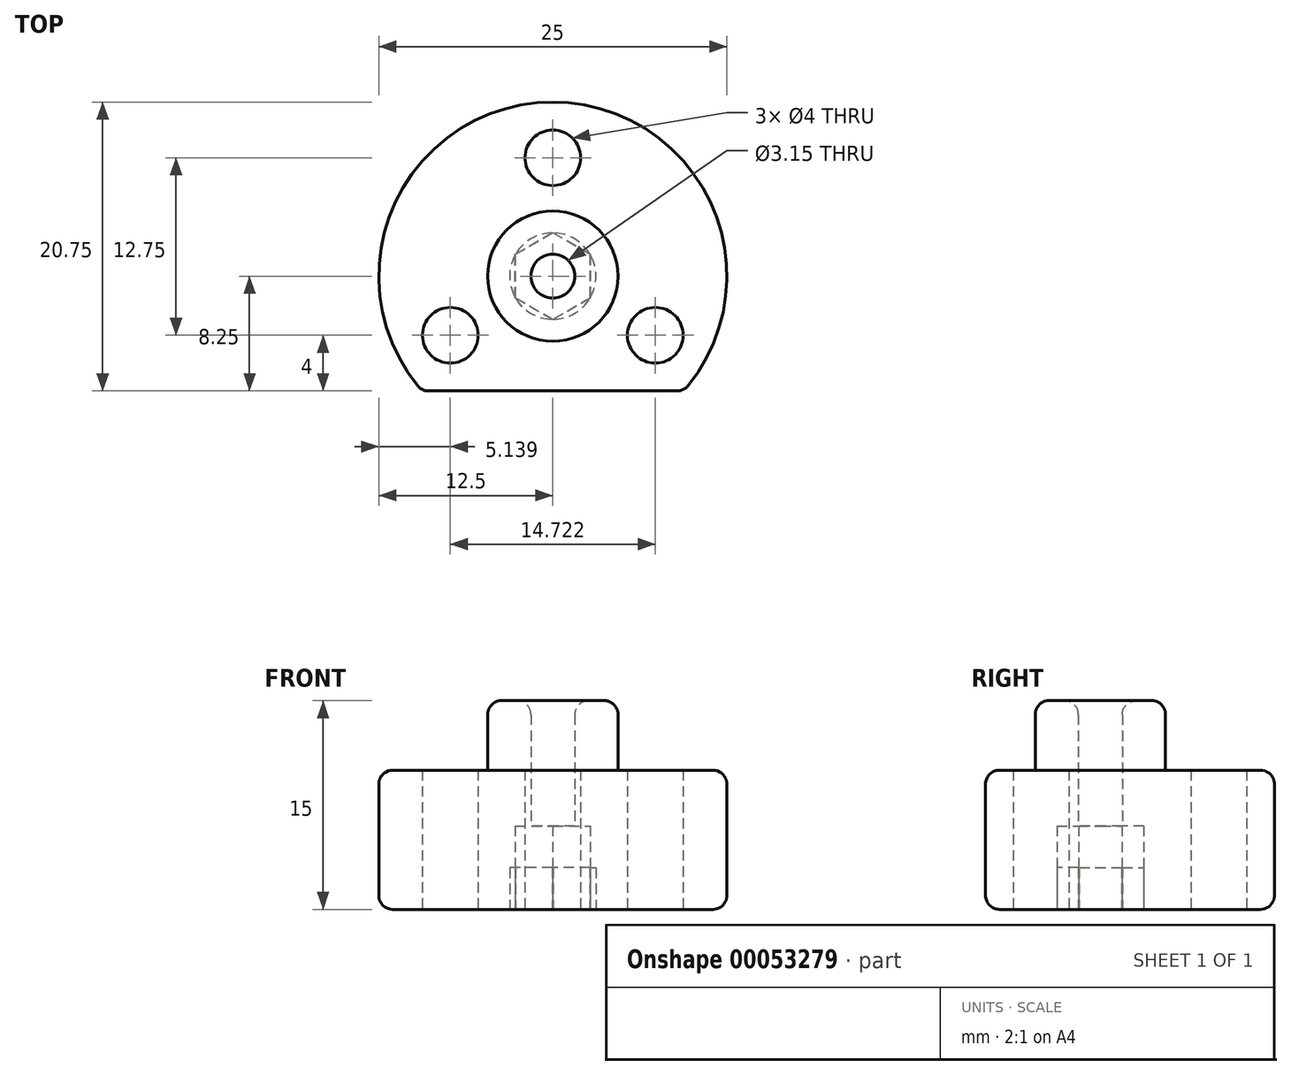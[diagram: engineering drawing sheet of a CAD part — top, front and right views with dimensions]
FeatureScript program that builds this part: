
annotation { "Feature Type Name" : "Feature", "Feature Type Description" : "" }
export const myFeature = defineFeature(function(context is Context, id is Id, definition is map)
    precondition{}
    {
        {
            var Q0;
            Q0=qCreatedBy(makeId("Top.planeOp"),FACE);
            var sketch = newSketch(context, id + "F0", { "sketchPlane" : qUnion([Q0])});
            skCircle(sketch, "E0", {"center": v(0, 0) * mm, "radius": 1.57 * mm});
            skCircle(sketch, "E1", {"center": v(0, 0) * mm, "radius": 8.5 * mm, "construction": true});
            skCircle(sketch, "E2", {"center": v(0, 0) * mm, "radius": 12.5 * mm});
            skCircle(sketch, "E3", {"center": v(0, 8.5) * mm, "radius": 2 * mm});
            skLineSegment(sketch, "E4", {"start": v(0, 0) * mm, "end": v(7.36, -4.25) * mm, "construction": true});
            skLineSegment(sketch, "E5", {"start": v(0, 0) * mm, "end": v(-7.36, -4.25) * mm, "construction": true});
            skLineSegment(sketch, "E6", {"start": v(-8.5, 0) * mm, "end": v(8.5, 0) * mm, "construction": true});
            skCircle(sketch, "E7", {"center": v(7.36, -4.25) * mm, "radius": 2 * mm});
            skCircle(sketch, "E8", {"center": v(-7.36, -4.25) * mm, "radius": 2 * mm});
            skLineSegment(sketch, "E9", {"start": v(7.36, -4.25) * mm, "end": v(7.36, -8.25) * mm, "construction": true});
            skLineSegment(sketch, "E10", {"start": v(-7.36, -4.25) * mm, "end": v(-7.36, -8.25) * mm, "construction": true});
            skLineSegment(sketch, "E11.top", {"start": v(9.4, -8.25) * mm, "end": v(-9.4, -8.25) * mm});
            skCircle(sketch, "E12", {"center": v(0, 0) * mm, "radius": 4.68 * mm});
            skCircle(sketch, "E13", {"center": v(0, 0) * mm, "radius": 3.1 * mm});
            skSolve(sketch);
        }
        {
            var Q0;
            Q0=makeQuery(id+"F0.imprint","IMPRINT",FACE,{"disambiguationData":[TD([[makeQuery(id+"F0.imprint","IMPRINT",EDGE,{"derivedFrom":sQuery(id+"F0.wireOp",EDGE,"E3")}),-1.0]])]});
            extrude(context, id + "F1", {"entities" : qUnion([Q0]), "depth" : 10 * mm});
        }
        {
            var Q0;
            Q0=makeQuery(id+"F0.imprint","IMPRINT",FACE,{"disambiguationData":[TD([[makeQuery(id+"F0.imprint","IMPRINT",EDGE,{"derivedFrom":sQuery(id+"F0.wireOp",EDGE,"E0")}),-1.0]])]});
            var Q1;
            Q1=makeQuery(id+"F0.imprint","IMPRINT",FACE,{"disambiguationData":[TD([[makeQuery(id+"F0.imprint","IMPRINT",EDGE,{"derivedFrom":sQuery(id+"F0.wireOp",EDGE,"E12")}),1.0]])]});
            extrude(context, id + "F2", {"entities" : qUnion([Q0, Q1]), "operationType" : NewBodyOperationType.ADD, "depth" : 15 * mm});
        }
        {
            var Q0;
            Q0=makeQuery(id+"F1.opExtrude","CAP_FACE",FACE,{"disambiguationData":[OSD([sQuery(id+"F0.wireOp",EDGE,"E2"),sQuery(id+"F0.wireOp",EDGE,"E3"),sQuery(id+"F0.wireOp",EDGE,"E7"),sQuery(id+"F0.wireOp",EDGE,"E8"),sQuery(id+"F0.wireOp",EDGE,"E11.top"),sQuery(id+"F0.wireOp",EDGE,"E12")])],"isStart":false});
            var Q1;
            Q1=makeQuery(id+"F0.imprint","IMPRINT",FACE,{"disambiguationData":[TD([[makeQuery(id+"F0.imprint","IMPRINT",EDGE,{"derivedFrom":sQuery(id+"F0.wireOp",EDGE,"E0")}),-1.0]])]});
            extrude(context, id + "F3", {"entities" : qUnion([Q0, Q1]), "operationType" : NewBodyOperationType.REMOVE, "depth" : 3 * mm});
        }
        {
            var Q0;
            Q0=qCreatedBy(makeId("Top.planeOp"),FACE);
            var sketch = newSketch(context, id + "F4", { "sketchPlane" : qUnion([Q0])});
            skCircle(sketch, "E14.cCircle", {"center": v(0, 0) * mm, "radius": 2.7 * mm, "construction": true});
            skLineSegment(sketch, "E14.0", {"start": v(2.7, 1.56) * mm, "end": v(2.7, -1.56) * mm});
            skLineSegment(sketch, "E14.1", {"start": v(2.7, -1.56) * mm, "end": v(0, -3.12) * mm});
            skLineSegment(sketch, "E14.2", {"start": v(0, -3.12) * mm, "end": v(-2.7, -1.56) * mm});
            skLineSegment(sketch, "E14.3", {"start": v(-2.7, -1.56) * mm, "end": v(-2.7, 1.56) * mm});
            skLineSegment(sketch, "E14.4", {"start": v(-2.7, 1.56) * mm, "end": v(0, 3.12) * mm});
            skLineSegment(sketch, "E14.5", {"start": v(0, 3.12) * mm, "end": v(2.7, 1.56) * mm});
            skPoint(sketch, "E14.0.midPoint", {"position": v(2.7, 0) * mm});
            skSolve(sketch);
        }
        {
            var Q0;
            Q0=makeQuery(id+"F4.imprint","IMPRINT",FACE,{"disambiguationData":[TD([[makeQuery(id+"F4.imprint","IMPRINT",EDGE,{"derivedFrom":sQuery(id+"F4.wireOp",EDGE,"E14.0")}),-1.0]])]});
            extrude(context, id + "F5", {"entities" : qUnion([Q0]), "operationType" : NewBodyOperationType.REMOVE, "depth" : 6 * mm});
        }
        {
            var Q0;
            Q0=makeQuery(id+"F2.opExtrude","CAP_EDGE",EDGE,{"disambiguationData":[OSD([sQuery(id+"F0.wireOp",EDGE,"E0")])],"isStart":false});
            var Q1;
            Q1=makeQuery(id+"F2.opExtrude","CAP_EDGE",EDGE,{"disambiguationData":[OSD([sQuery(id+"F0.wireOp",EDGE,"E12")])],"isStart":false});
            var Q2;
            Q2=makeQuery(id+"F1.opExtrude","CAP_EDGE",EDGE,{"disambiguationData":[OSD([sQuery(id+"F0.wireOp",EDGE,"E12")])],"isStart":false});
            var Q3;
            Q3=makeQuery(id+"F1.opExtrude","CAP_EDGE",EDGE,{"disambiguationData":[OSD([sQuery(id+"F0.wireOp",EDGE,"E2")])],"isStart":false});
            var Q4;
            Q4=makeQuery(id+"F1.opExtrude","CAP_EDGE",EDGE,{"disambiguationData":[OSD([sQuery(id+"F0.wireOp",EDGE,"E11.top")])],"isStart":false});
            var Q5;
            Q5=makeQuery(id+"F1.opExtrude","CAP_EDGE",EDGE,{"disambiguationData":[OSD([sQuery(id+"F0.wireOp",EDGE,"E2")])],"isStart":true});
            var Q6;
            Q6=makeQuery(id+"F1.opExtrude","CAP_EDGE",EDGE,{"disambiguationData":[OSD([sQuery(id+"F0.wireOp",EDGE,"E11.top")])],"isStart":true});
            var Q7;
            {var subQ0=sQuery(id+"F0.wireOp",EDGE,"E11.top");var subQ1=sQuery(id+"F0.wireOp",EDGE,"E2");Q7=makeQuery(id+"F1.opExtrude","SWEPT_EDGE",EDGE,{"disambiguationData":[OSD([subQ1,subQ0]),TDD([makeQuery(id+"F0.imprint","INTERSECT",VERTEX,{"disambiguationData":[OD(1.0)],"derivedFrom":[subQ1,subQ0]})])]});}
            var Q8;
            {var subQ0=sQuery(id+"F0.wireOp",EDGE,"E11.top");var subQ1=sQuery(id+"F0.wireOp",EDGE,"E2");Q8=makeQuery(id+"F1.opExtrude","SWEPT_EDGE",EDGE,{"disambiguationData":[OSD([subQ1,subQ0]),TDD([makeQuery(id+"F0.imprint","INTERSECT",VERTEX,{"disambiguationData":[OD(0.0)],"derivedFrom":[subQ1,subQ0]})])]});}
            fillet(context, id + "F6", {"entities" : qUnion([Q0, Q1, Q2, Q3, Q4, Q5, Q6, Q7, Q8]), "radius" : 1 * mm, "tangentPropagation" : true, "allowEdgeOverflow" : false});
        }
    });
